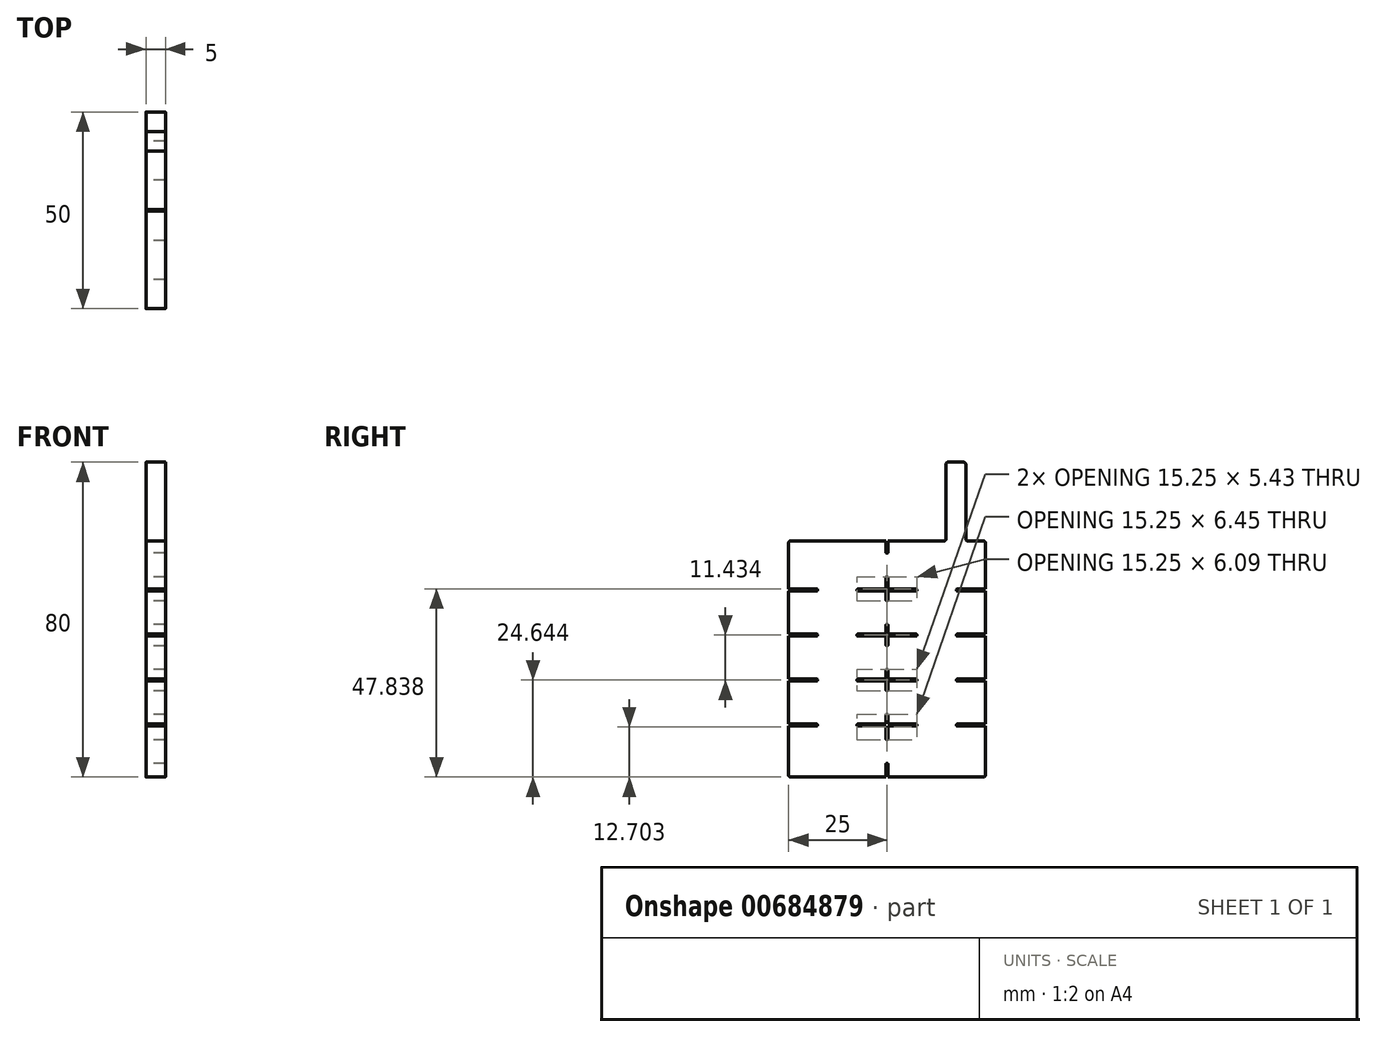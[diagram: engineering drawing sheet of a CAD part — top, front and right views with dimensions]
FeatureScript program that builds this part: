
annotation { "Feature Type Name" : "Feature", "Feature Type Description" : "" }
export const myFeature = defineFeature(function(context is Context, id is Id, definition is map)
    precondition{}
    {
        {
            var Q0;
            Q0=qCreatedBy(makeId("Right.planeOp"),FACE);
            var sketch = newSketch(context, id + "F0", { "sketchPlane" : qUnion([Q0])});
            skPoint(sketch, "E0.0", {"position": v(0, 0) * mm});
            skLineSegment(sketch, "E1.bottom", {"start": v(0, 0) * mm, "end": v(12.38, 0) * mm});
            skLineSegment(sketch, "E1.top", {"start": v(0, -60) * mm, "end": v(24.75, -60) * mm});
            skLineSegment(sketch, "E1.left", {"start": v(0, 0) * mm, "end": v(0, -12.24) * mm});
            skLineSegment(sketch, "E1.right", {"start": v(50, 0) * mm, "end": v(50, -12.24) * mm});
            skPoint(sketch, "E2.MirrorP", {"position": v(11.5, 0) * mm});
            skPoint(sketch, "E3.MirrorP", {"position": v(11.5, -2) * mm});
            skPoint(sketch, "E4.MirrorP", {"position": v(18.5, 0) * mm});
            skPoint(sketch, "E5.MirrorP", {"position": v(30, 0) * mm});
            skLineSegment(sketch, "E6.0", {"start": v(25.25, -60) * mm, "end": v(25.25, -56.52) * mm});
            skLineSegment(sketch, "E7.0", {"start": v(0, -12.24) * mm, "end": v(7.38, -12.24) * mm});
            skLineSegment(sketch, "E8.0", {"start": v(0, -12.74) * mm, "end": v(7.38, -12.74) * mm});
            skLineSegment(sketch, "E9.trimOffspring", {"start": v(25.25, -3.12) * mm, "end": v(25.25, -1.3) * mm});
            skLineSegment(sketch, "E10.trimOffspring", {"start": v(25.25, -12.24) * mm, "end": v(32.63, -12.24) * mm});
            skLineSegment(sketch, "E11.trimOffspring", {"start": v(25.25, -12.24) * mm, "end": v(25.25, -9.12) * mm});
            skLineSegment(sketch, "E12.trimOffspring", {"start": v(25.25, -12.74) * mm, "end": v(32.63, -12.74) * mm});
            skLineSegment(sketch, "E13.trimOffspring", {"start": v(25.25, -15.2) * mm, "end": v(25.25, -12.74) * mm});
            skLineSegment(sketch, "E14.0", {"start": v(0, -23.67) * mm, "end": v(7.38, -23.67) * mm});
            skLineSegment(sketch, "E15.0", {"start": v(0, -24.17) * mm, "end": v(7.38, -24.17) * mm});
            skLineSegment(sketch, "E16.trimOffspring", {"start": v(25.25, -23.67) * mm, "end": v(32.63, -23.67) * mm});
            skLineSegment(sketch, "E17.trimOffspring", {"start": v(25.25, -23.67) * mm, "end": v(25.25, -21.2) * mm});
            skLineSegment(sketch, "E18.trimOffspring", {"start": v(25.25, -24.17) * mm, "end": v(32.63, -24.17) * mm});
            skLineSegment(sketch, "E19.trimOffspring", {"start": v(25.25, -26.64) * mm, "end": v(25.25, -24.17) * mm});
            skLineSegment(sketch, "E20.trimOffspring", {"start": v(24.75, -26.64) * mm, "end": v(24.75, -24.17) * mm});
            skLineSegment(sketch, "E21.0", {"start": v(0, -35.1) * mm, "end": v(7.38, -35.1) * mm});
            skLineSegment(sketch, "E22.0", {"start": v(0, -35.6) * mm, "end": v(7.38, -35.6) * mm});
            skLineSegment(sketch, "E23.trimOffspring", {"start": v(25.25, -35.1) * mm, "end": v(32.63, -35.1) * mm});
            skLineSegment(sketch, "E24.trimOffspring", {"start": v(25.25, -35.1) * mm, "end": v(25.25, -32.64) * mm});
            skLineSegment(sketch, "E25.trimOffspring", {"start": v(24.75, -35.1) * mm, "end": v(24.75, -32.64) * mm});
            skLineSegment(sketch, "E26.trimOffspring", {"start": v(25.25, -35.6) * mm, "end": v(32.63, -35.6) * mm});
            skLineSegment(sketch, "E27.trimOffspring", {"start": v(25.25, -38.07) * mm, "end": v(25.25, -35.6) * mm});
            skLineSegment(sketch, "E28.trimOffspring", {"start": v(24.75, -38.07) * mm, "end": v(24.75, -35.6) * mm});
            skLineSegment(sketch, "E29.0", {"start": v(0, -46.54) * mm, "end": v(7.38, -46.54) * mm});
            skLineSegment(sketch, "E30.0", {"start": v(0, -47.04) * mm, "end": v(7.38, -47.04) * mm});
            skLineSegment(sketch, "E31.trimOffspring", {"start": v(25.25, -46.54) * mm, "end": v(32.63, -46.54) * mm});
            skLineSegment(sketch, "E32.trimOffspring", {"start": v(25.25, -46.54) * mm, "end": v(25.25, -44.07) * mm});
            skLineSegment(sketch, "E33.trimOffspring", {"start": v(24.75, -46.54) * mm, "end": v(24.75, -44.07) * mm});
            skLineSegment(sketch, "E34.trimOffspring", {"start": v(25.25, -47.04) * mm, "end": v(32.63, -47.04) * mm});
            skLineSegment(sketch, "E35.trimOffspring", {"start": v(25.25, -50.52) * mm, "end": v(25.25, -47.04) * mm});
            skLineSegment(sketch, "E36.trimOffspring", {"start": v(0, -12.74) * mm, "end": v(0, -23.67) * mm});
            skLineSegment(sketch, "E37.trimOffspring", {"start": v(0, -24.17) * mm, "end": v(0, -35.1) * mm});
            skLineSegment(sketch, "E38.trimOffspring", {"start": v(0, -35.6) * mm, "end": v(0, -46.54) * mm});
            skLineSegment(sketch, "E39.trimOffspring", {"start": v(0, -47.04) * mm, "end": v(0, -60) * mm});
            skLineSegment(sketch, "E40.trimOffspring", {"start": v(50, -47.04) * mm, "end": v(50, -60) * mm});
            skLineSegment(sketch, "E41.trimOffspring", {"start": v(50, -35.6) * mm, "end": v(50, -46.54) * mm});
            skLineSegment(sketch, "E42.trimOffspring", {"start": v(50, -12.74) * mm, "end": v(50, -23.67) * mm});
            skLineSegment(sketch, "E43.trimOffspring", {"start": v(50, -24.17) * mm, "end": v(50, -35.1) * mm});
            skLineSegment(sketch, "E44.0", {"start": v(17.38, -12.74) * mm, "end": v(17.38, -12.24) * mm});
            skLineSegment(sketch, "E45.0", {"start": v(7.38, -12.74) * mm, "end": v(7.38, -12.24) * mm});
            skLineSegment(sketch, "E46", {"start": v(24.75, -12.24) * mm, "end": v(24.75, -9.12) * mm});
            skLineSegment(sketch, "E47.0", {"start": v(24.75, -9.12) * mm, "end": v(25.25, -9.12) * mm});
            skLineSegment(sketch, "E48.0", {"start": v(24.75, -3.12) * mm, "end": v(25.25, -3.12) * mm});
            skLineSegment(sketch, "E49", {"start": v(24.75, -12.74) * mm, "end": v(24.75, -15.2) * mm});
            skLineSegment(sketch, "E50.0", {"start": v(24.75, -21.2) * mm, "end": v(25.25, -21.2) * mm});
            skLineSegment(sketch, "E51.0", {"start": v(24.75, -15.2) * mm, "end": v(25.25, -15.2) * mm});
            skLineSegment(sketch, "E52", {"start": v(25.25, -1.3) * mm, "end": v(25.25, 0) * mm});
            skLineSegment(sketch, "E53.trimOffspring", {"start": v(25.25, 0) * mm, "end": v(35.12, 0) * mm});
            skPoint(sketch, "E54.start.orphan", {"position": v(24.75, -6.12) * mm});
            skLineSegment(sketch, "E55", {"start": v(7.38, -12.24) * mm, "end": v(7.38, -12.74) * mm});
            skLineSegment(sketch, "E56", {"start": v(17.38, -12.24) * mm, "end": v(17.38, -12.74) * mm});
            skLineSegment(sketch, "E57.trimOffspring", {"start": v(7.38, -23.67) * mm, "end": v(7.38, -24.17) * mm});
            skLineSegment(sketch, "E58.trimOffspring", {"start": v(17.38, -23.67) * mm, "end": v(17.38, -24.17) * mm});
            skLineSegment(sketch, "E59.trimOffspring", {"start": v(7.38, -35.1) * mm, "end": v(7.38, -35.6) * mm});
            skLineSegment(sketch, "E60.trimOffspring", {"start": v(17.38, -35.1) * mm, "end": v(17.38, -35.6) * mm});
            skLineSegment(sketch, "E61.trimOffspring", {"start": v(7.38, -46.54) * mm, "end": v(7.38, -47.04) * mm});
            skLineSegment(sketch, "E62.trimOffspring", {"start": v(17.38, -46.54) * mm, "end": v(17.38, -47.04) * mm});
            skLineSegment(sketch, "E63.trimOffspring", {"start": v(17.38, -46.54) * mm, "end": v(24.75, -46.54) * mm});
            skLineSegment(sketch, "E64.trimOffspring", {"start": v(17.38, -47.04) * mm, "end": v(24.75, -47.04) * mm});
            skLineSegment(sketch, "E65.trimOffspring", {"start": v(17.38, -35.1) * mm, "end": v(24.75, -35.1) * mm});
            skLineSegment(sketch, "E66.trimOffspring", {"start": v(17.38, -35.6) * mm, "end": v(24.75, -35.6) * mm});
            skLineSegment(sketch, "E67.trimOffspring", {"start": v(17.37, -23.67) * mm, "end": v(24.75, -23.67) * mm});
            skLineSegment(sketch, "E68.trimOffspring", {"start": v(17.37, -24.17) * mm, "end": v(24.75, -24.17) * mm});
            skLineSegment(sketch, "E69.trimOffspring", {"start": v(17.38, -12.24) * mm, "end": v(24.75, -12.24) * mm});
            skPoint(sketch, "E70.start.orphan", {"position": v(12.38, -12.74) * mm});
            skPoint(sketch, "E71.orphan", {"position": v(12.38, -12.24) * mm});
            skLineSegment(sketch, "E72.trimOffspring", {"start": v(17.38, -12.74) * mm, "end": v(24.75, -12.74) * mm});
            skLineSegment(sketch, "E73.0", {"start": v(32.63, -12.24) * mm, "end": v(32.63, -12.74) * mm});
            skLineSegment(sketch, "E74.0", {"start": v(42.62, -12.24) * mm, "end": v(42.62, -12.74) * mm});
            skLineSegment(sketch, "E75.trimOffspring", {"start": v(32.63, -23.67) * mm, "end": v(32.63, -24.17) * mm});
            skLineSegment(sketch, "E76.trimOffspring", {"start": v(42.62, -23.67) * mm, "end": v(42.62, -24.17) * mm});
            skLineSegment(sketch, "E77.trimOffspring", {"start": v(32.63, -35.1) * mm, "end": v(32.63, -35.6) * mm});
            skLineSegment(sketch, "E78.trimOffspring", {"start": v(42.62, -35.1) * mm, "end": v(42.62, -35.6) * mm});
            skLineSegment(sketch, "E79.trimOffspring", {"start": v(32.63, -46.54) * mm, "end": v(32.63, -47.04) * mm});
            skLineSegment(sketch, "E80.trimOffspring", {"start": v(42.62, -46.54) * mm, "end": v(42.62, -47.04) * mm});
            skLineSegment(sketch, "E81.0", {"start": v(24.75, -26.64) * mm, "end": v(25.25, -26.64) * mm});
            skLineSegment(sketch, "E82.0", {"start": v(24.75, -32.64) * mm, "end": v(25.25, -32.64) * mm});
            skLineSegment(sketch, "E83.0", {"start": v(24.75, -38.07) * mm, "end": v(25.25, -38.07) * mm});
            skLineSegment(sketch, "E84.0", {"start": v(24.75, -44.07) * mm, "end": v(25.25, -44.07) * mm});
            skLineSegment(sketch, "E85", {"start": v(24.75, -47.04) * mm, "end": v(24.75, -50.52) * mm});
            skLineSegment(sketch, "E86.0", {"start": v(24.75, -56.52) * mm, "end": v(25.25, -56.52) * mm});
            skLineSegment(sketch, "E87.0", {"start": v(24.75, -50.52) * mm, "end": v(25.25, -50.52) * mm});
            skLineSegment(sketch, "E88.trimOffspring", {"start": v(24.75, -56.52) * mm, "end": v(24.75, -60) * mm});
            skLineSegment(sketch, "E89.trimOffspring", {"start": v(25.25, -60) * mm, "end": v(50, -60) * mm});
            skLineSegment(sketch, "E90.trimOffspring", {"start": v(42.62, -46.54) * mm, "end": v(50, -46.54) * mm});
            skLineSegment(sketch, "E91.trimOffspring", {"start": v(42.62, -47.04) * mm, "end": v(50, -47.04) * mm});
            skLineSegment(sketch, "E92.trimOffspring", {"start": v(42.62, -35.1) * mm, "end": v(50, -35.1) * mm});
            skLineSegment(sketch, "E93.trimOffspring", {"start": v(42.62, -35.6) * mm, "end": v(50, -35.6) * mm});
            skLineSegment(sketch, "E94.trimOffspring", {"start": v(42.62, -23.67) * mm, "end": v(50, -23.67) * mm});
            skLineSegment(sketch, "E95.trimOffspring", {"start": v(42.62, -24.17) * mm, "end": v(50, -24.17) * mm});
            skLineSegment(sketch, "E96.trimOffspring", {"start": v(42.62, -12.24) * mm, "end": v(50, -12.24) * mm});
            skLineSegment(sketch, "E97.trimOffspring", {"start": v(42.62, -12.74) * mm, "end": v(50, -12.74) * mm});
            skLineSegment(sketch, "E98.trimOffspring", {"start": v(24.75, -21.2) * mm, "end": v(24.75, -23.67) * mm});
            skPoint(sketch, "E99.end.orphan", {"position": v(25.25, -18.2) * mm});
            skPoint(sketch, "E99.start.orphan", {"position": v(24.75, -18.2) * mm});
            skPoint(sketch, "E100.orphan", {"position": v(25.25, -17.95) * mm});
            skPoint(sketch, "E101.end.orphan", {"position": v(25.25, -18.45) * mm});
            skLineSegment(sketch, "E102.trimOffspring", {"start": v(24.75, -3.12) * mm, "end": v(24.75, 0) * mm});
            skPoint(sketch, "E103.orphan", {"position": v(14.88, 25) * mm});
            skPoint(sketch, "E104.orphan", {"position": v(37.63, 25) * mm});
            skLineSegment(sketch, "E105.trimOffspring", {"start": v(14.88, 0) * mm, "end": v(24.75, 0) * mm});
            skLineSegment(sketch, "E106.trimOffspring", {"start": v(37.63, 0) * mm, "end": v(40, 0) * mm});
            skLineSegment(sketch, "E107", {"start": v(35.12, 0) * mm, "end": v(40, 0) * mm});
            skLineSegment(sketch, "E108.0", {"start": v(45, 0) * mm, "end": v(45, 15) * mm});
            skLineSegment(sketch, "E109.0", {"start": v(40, 0) * mm, "end": v(40, 15) * mm});
            skLineSegment(sketch, "E110", {"start": v(14.88, 0) * mm, "end": v(11.5, 0) * mm});
            skLineSegment(sketch, "E111.trimOffspring", {"start": v(45, 0) * mm, "end": v(50, 0) * mm});
            skLineSegment(sketch, "E112.0", {"start": v(40, 20) * mm, "end": v(45, 20) * mm});
            skLineSegment(sketch, "E113", {"start": v(40, 20) * mm, "end": v(40, 15) * mm});
            skLineSegment(sketch, "E114", {"start": v(45, 20) * mm, "end": v(45, 15) * mm});
            skSolve(sketch);
        }
        {
            var Q0;
            {var subQ1=sQuery(id+"F0.wireOp",EDGE,"6f222dcf-cafe-427f-96f1-de862232ba62.0");Q0=makeQuery(id+"F0.imprint","IMPRINT",FACE,{"disambiguationData":[TD([[makeQuery(id+"F0.imprint","IMPRINT",EDGE,{"derivedFrom":subQ1}),-1.0]])]});}
            var Q1;
            {var subQ1=sQuery(id+"F0.wireOp",EDGE,"9ddca581-0f96-48d2-9b8e-d0e5be099db1.trimOffspring");Q1=makeQuery(id+"F0.imprint","IMPRINT",FACE,{"disambiguationData":[TD([[makeQuery(id+"F0.imprint","IMPRINT",EDGE,{"derivedFrom":subQ1}),-1.0]])]});}
            var Q2;
            Q2=makeQuery(id+"F0.imprint","IMPRINT",FACE,{"disambiguationData":[TD([[makeQuery(id+"F0.imprint","IMPRINT",EDGE,{"derivedFrom":sQuery(id+"F0.wireOp",EDGE,"E8.0")}),-1.0]])]});
            var Q3;
            Q3=makeQuery(id+"F0.imprint","IMPRINT",FACE,{"disambiguationData":[TD([[makeQuery(id+"F0.imprint","IMPRINT",EDGE,{"derivedFrom":sQuery(id+"F0.wireOp",EDGE,"E12.trimOffspring")}),-1.0]])]});
            var Q4;
            Q4=makeQuery(id+"F0.imprint","IMPRINT",FACE,{"disambiguationData":[TD([[makeQuery(id+"F0.imprint","IMPRINT",EDGE,{"derivedFrom":sQuery(id+"F0.wireOp",EDGE,"E18.trimOffspring")}),-1.0]])]});
            var Q5;
            Q5=makeQuery(id+"F0.imprint","IMPRINT",FACE,{"disambiguationData":[TD([[makeQuery(id+"F0.imprint","IMPRINT",EDGE,{"derivedFrom":sQuery(id+"F0.wireOp",EDGE,"E15.0")}),-1.0]])]});
            var Q6;
            Q6=makeQuery(id+"F0.imprint","IMPRINT",FACE,{"disambiguationData":[TD([[makeQuery(id+"F0.imprint","IMPRINT",EDGE,{"derivedFrom":sQuery(id+"F0.wireOp",EDGE,"E22.0")}),-1.0]])]});
            var Q7;
            Q7=makeQuery(id+"F0.imprint","IMPRINT",FACE,{"disambiguationData":[TD([[makeQuery(id+"F0.imprint","IMPRINT",EDGE,{"derivedFrom":sQuery(id+"F0.wireOp",EDGE,"E26.trimOffspring")}),-1.0]])]});
            var Q8;
            {var subQ0=sQuery(id+"F0.wireOp",EDGE,"E6.0");Q8=makeQuery(id+"F0.imprint","IMPRINT",FACE,{"disambiguationData":[TD([[makeQuery(id+"F0.imprint","IMPRINT",EDGE,{"derivedFrom":subQ0}),-1.0]])]});}
            var Q9;
            {var subQ0=sQuery(id+"F0.wireOp",EDGE,"52d86100-12cc-4532-affd-39e9c9b04a49.0");Q9=makeQuery(id+"F0.imprint","IMPRINT",FACE,{"disambiguationData":[TD([[makeQuery(id+"F0.imprint","IMPRINT",EDGE,{"derivedFrom":subQ0}),1.0]])]});}
            extrude(context, id + "F1", {"entities" : qUnion([Q0, Q1, Q2, Q3, Q4, Q5, Q6, Q7, Q8, Q9]), "depth" : 5 * mm, "offsetDistance" : 25 * mm});
        }
        {
            var Q0;
            Q0=makeQuery(id+"F1.opExtrude","SWEPT_EDGE",EDGE,{"disambiguationData":[OSD([sQuery(id+"F0.wireOp",EDGE,"E1.bottom"),sQuery(id+"F0.wireOp",EDGE,"E1.left")])]});
            var Q1;
            Q1=makeQuery(id+"F1.opExtrude","SWEPT_EDGE",EDGE,{"disambiguationData":[OSD([sQuery(id+"F0.wireOp",EDGE,"E1.right"),sQuery(id+"F0.wireOp",EDGE,"E111.trimOffspring")])]});
            var Q2;
            Q2=makeQuery(id+"F1.opExtrude","SWEPT_EDGE",EDGE,{"disambiguationData":[OSD([sQuery(id+"F0.wireOp",EDGE,"E40.trimOffspring"),sQuery(id+"F0.wireOp",EDGE,"E89.trimOffspring")])]});
            var Q3;
            Q3=makeQuery(id+"F1.opExtrude","SWEPT_EDGE",EDGE,{"disambiguationData":[OSD([sQuery(id+"F0.wireOp",EDGE,"E1.top"),sQuery(id+"F0.wireOp",EDGE,"E39.trimOffspring")])]});
            fillet(context, id + "F2", {"entities" : qUnion([Q0, Q1, Q2, Q3]), "radius" : 0.5 * mm, "tangentPropagation" : true, "allowEdgeOverflow" : false});
        }
        {
            var Q0;
            Q0=makeQuery(id+"F1.opExtrude","SWEPT_EDGE",EDGE,{"disambiguationData":[OSD([sQuery(id+"F0.wireOp",EDGE,"E112.0"),sQuery(id+"F0.wireOp",EDGE,"E114")])]});
            var Q1;
            Q1=makeQuery(id+"F1.opExtrude","SWEPT_EDGE",EDGE,{"disambiguationData":[OSD([sQuery(id+"F0.wireOp",EDGE,"E112.0"),sQuery(id+"F0.wireOp",EDGE,"E113")])]});
            fillet(context, id + "F3", {"entities" : qUnion([Q0, Q1]), "radius" : 0.5 * mm, "tangentPropagation" : true, "allowEdgeOverflow" : false});
        }
        {
            var Q0;
            Q0=makeQuery(id+"F1.opExtrude","SWEPT_EDGE",EDGE,{"disambiguationData":[OSD([sQuery(id+"F0.wireOp",EDGE,"E107"),sQuery(id+"F0.wireOp",EDGE,"E109.0")])]});
            var Q1;
            Q1=makeQuery(id+"F1.opExtrude","SWEPT_EDGE",EDGE,{"disambiguationData":[OSD([sQuery(id+"F0.wireOp",EDGE,"E108.0"),sQuery(id+"F0.wireOp",EDGE,"E111.trimOffspring")])]});
            fillet(context, id + "F4", {"entities" : qUnion([Q0, Q1]), "radius" : 0.5 * mm, "tangentPropagation" : true, "allowEdgeOverflow" : false});
        }
        {
            var Q0;
            Q0=makeQuery(id+"F1.opExtrude","SWEPT_EDGE",EDGE,{"disambiguationData":[OSD([sQuery(id+"F0.wireOp",EDGE,"E9.trimOffspring"),sQuery(id+"F0.wireOp",EDGE,"E48.0")])]});
            var Q1;
            Q1=makeQuery(id+"F1.opExtrude","SWEPT_EDGE",EDGE,{"disambiguationData":[OSD([sQuery(id+"F0.wireOp",EDGE,"E48.0"),sQuery(id+"F0.wireOp",EDGE,"E102.trimOffspring")])]});
            var Q2;
            Q2=makeQuery(id+"F1.opExtrude","SWEPT_EDGE",EDGE,{"disambiguationData":[OSD([sQuery(id+"F0.wireOp",EDGE,"E74.0"),sQuery(id+"F0.wireOp",EDGE,"E96.trimOffspring")])]});
            var Q3;
            Q3=makeQuery(id+"F1.opExtrude","SWEPT_EDGE",EDGE,{"disambiguationData":[OSD([sQuery(id+"F0.wireOp",EDGE,"E74.0"),sQuery(id+"F0.wireOp",EDGE,"E97.trimOffspring")])]});
            var Q4;
            Q4=makeQuery(id+"F1.opExtrude","SWEPT_EDGE",EDGE,{"disambiguationData":[OSD([sQuery(id+"F0.wireOp",EDGE,"E76.trimOffspring"),sQuery(id+"F0.wireOp",EDGE,"E94.trimOffspring")])]});
            var Q5;
            Q5=makeQuery(id+"F1.opExtrude","SWEPT_EDGE",EDGE,{"disambiguationData":[OSD([sQuery(id+"F0.wireOp",EDGE,"E76.trimOffspring"),sQuery(id+"F0.wireOp",EDGE,"E95.trimOffspring")])]});
            var Q6;
            Q6=makeQuery(id+"F1.opExtrude","SWEPT_EDGE",EDGE,{"disambiguationData":[OSD([sQuery(id+"F0.wireOp",EDGE,"E78.trimOffspring"),sQuery(id+"F0.wireOp",EDGE,"E92.trimOffspring")])]});
            var Q7;
            Q7=makeQuery(id+"F1.opExtrude","SWEPT_EDGE",EDGE,{"disambiguationData":[OSD([sQuery(id+"F0.wireOp",EDGE,"E78.trimOffspring"),sQuery(id+"F0.wireOp",EDGE,"E93.trimOffspring")])]});
            var Q8;
            Q8=makeQuery(id+"F1.opExtrude","SWEPT_EDGE",EDGE,{"disambiguationData":[OSD([sQuery(id+"F0.wireOp",EDGE,"E80.trimOffspring"),sQuery(id+"F0.wireOp",EDGE,"E90.trimOffspring")])]});
            var Q9;
            Q9=makeQuery(id+"F1.opExtrude","SWEPT_EDGE",EDGE,{"disambiguationData":[OSD([sQuery(id+"F0.wireOp",EDGE,"E80.trimOffspring"),sQuery(id+"F0.wireOp",EDGE,"E91.trimOffspring")])]});
            var Q10;
            Q10=makeQuery(id+"F1.opExtrude","SWEPT_EDGE",EDGE,{"disambiguationData":[OSD([sQuery(id+"F0.wireOp",EDGE,"E86.0"),sQuery(id+"F0.wireOp",EDGE,"E88.trimOffspring")])]});
            var Q11;
            Q11=makeQuery(id+"F1.opExtrude","SWEPT_EDGE",EDGE,{"disambiguationData":[OSD([sQuery(id+"F0.wireOp",EDGE,"E6.0"),sQuery(id+"F0.wireOp",EDGE,"E86.0")])]});
            var Q12;
            Q12=makeQuery(id+"F1.opExtrude","SWEPT_EDGE",EDGE,{"disambiguationData":[OSD([sQuery(id+"F0.wireOp",EDGE,"E85"),sQuery(id+"F0.wireOp",EDGE,"E87.0")])]});
            var Q13;
            Q13=makeQuery(id+"F1.opExtrude","SWEPT_EDGE",EDGE,{"disambiguationData":[OSD([sQuery(id+"F0.wireOp",EDGE,"E35.trimOffspring"),sQuery(id+"F0.wireOp",EDGE,"E87.0")])]});
            var Q14;
            Q14=makeQuery(id+"F1.opExtrude","SWEPT_EDGE",EDGE,{"disambiguationData":[OSD([sQuery(id+"F0.wireOp",EDGE,"E34.trimOffspring"),sQuery(id+"F0.wireOp",EDGE,"E79.trimOffspring")])]});
            var Q15;
            Q15=makeQuery(id+"F1.opExtrude","SWEPT_EDGE",EDGE,{"disambiguationData":[OSD([sQuery(id+"F0.wireOp",EDGE,"E31.trimOffspring"),sQuery(id+"F0.wireOp",EDGE,"E79.trimOffspring")])]});
            var Q16;
            Q16=makeQuery(id+"F1.opExtrude","SWEPT_EDGE",EDGE,{"disambiguationData":[OSD([sQuery(id+"F0.wireOp",EDGE,"E32.trimOffspring"),sQuery(id+"F0.wireOp",EDGE,"E84.0")])]});
            var Q17;
            Q17=makeQuery(id+"F1.opExtrude","SWEPT_EDGE",EDGE,{"disambiguationData":[OSD([sQuery(id+"F0.wireOp",EDGE,"E33.trimOffspring"),sQuery(id+"F0.wireOp",EDGE,"E84.0")])]});
            var Q18;
            Q18=makeQuery(id+"F1.opExtrude","SWEPT_EDGE",EDGE,{"disambiguationData":[OSD([sQuery(id+"F0.wireOp",EDGE,"E62.trimOffspring"),sQuery(id+"F0.wireOp",EDGE,"E63.trimOffspring")])]});
            var Q19;
            Q19=makeQuery(id+"F1.opExtrude","SWEPT_EDGE",EDGE,{"disambiguationData":[OSD([sQuery(id+"F0.wireOp",EDGE,"E62.trimOffspring"),sQuery(id+"F0.wireOp",EDGE,"E64.trimOffspring")])]});
            var Q20;
            Q20=makeQuery(id+"F1.opExtrude","SWEPT_EDGE",EDGE,{"disambiguationData":[OSD([sQuery(id+"F0.wireOp",EDGE,"E28.trimOffspring"),sQuery(id+"F0.wireOp",EDGE,"E83.0")])]});
            var Q21;
            Q21=makeQuery(id+"F1.opExtrude","SWEPT_EDGE",EDGE,{"disambiguationData":[OSD([sQuery(id+"F0.wireOp",EDGE,"E27.trimOffspring"),sQuery(id+"F0.wireOp",EDGE,"E83.0")])]});
            var Q22;
            Q22=makeQuery(id+"F1.opExtrude","SWEPT_EDGE",EDGE,{"disambiguationData":[OSD([sQuery(id+"F0.wireOp",EDGE,"E26.trimOffspring"),sQuery(id+"F0.wireOp",EDGE,"E77.trimOffspring")])]});
            var Q23;
            Q23=makeQuery(id+"F1.opExtrude","SWEPT_EDGE",EDGE,{"disambiguationData":[OSD([sQuery(id+"F0.wireOp",EDGE,"E23.trimOffspring"),sQuery(id+"F0.wireOp",EDGE,"E77.trimOffspring")])]});
            var Q24;
            Q24=makeQuery(id+"F1.opExtrude","SWEPT_EDGE",EDGE,{"disambiguationData":[OSD([sQuery(id+"F0.wireOp",EDGE,"E24.trimOffspring"),sQuery(id+"F0.wireOp",EDGE,"E82.0")])]});
            var Q25;
            Q25=makeQuery(id+"F1.opExtrude","SWEPT_EDGE",EDGE,{"disambiguationData":[OSD([sQuery(id+"F0.wireOp",EDGE,"E25.trimOffspring"),sQuery(id+"F0.wireOp",EDGE,"E82.0")])]});
            var Q26;
            Q26=makeQuery(id+"F1.opExtrude","SWEPT_EDGE",EDGE,{"disambiguationData":[OSD([sQuery(id+"F0.wireOp",EDGE,"E60.trimOffspring"),sQuery(id+"F0.wireOp",EDGE,"E66.trimOffspring")])]});
            var Q27;
            Q27=makeQuery(id+"F1.opExtrude","SWEPT_EDGE",EDGE,{"disambiguationData":[OSD([sQuery(id+"F0.wireOp",EDGE,"E60.trimOffspring"),sQuery(id+"F0.wireOp",EDGE,"E65.trimOffspring")])]});
            var Q28;
            Q28=makeQuery(id+"F1.opExtrude","SWEPT_EDGE",EDGE,{"disambiguationData":[OSD([sQuery(id+"F0.wireOp",EDGE,"E58.trimOffspring"),sQuery(id+"F0.wireOp",EDGE,"E67.trimOffspring")])]});
            var Q29;
            Q29=makeQuery(id+"F1.opExtrude","SWEPT_EDGE",EDGE,{"disambiguationData":[OSD([sQuery(id+"F0.wireOp",EDGE,"E58.trimOffspring"),sQuery(id+"F0.wireOp",EDGE,"E68.trimOffspring")])]});
            var Q30;
            Q30=makeQuery(id+"F1.opExtrude","SWEPT_EDGE",EDGE,{"disambiguationData":[OSD([sQuery(id+"F0.wireOp",EDGE,"E20.trimOffspring"),sQuery(id+"F0.wireOp",EDGE,"E81.0")])]});
            var Q31;
            Q31=makeQuery(id+"F1.opExtrude","SWEPT_EDGE",EDGE,{"disambiguationData":[OSD([sQuery(id+"F0.wireOp",EDGE,"E19.trimOffspring"),sQuery(id+"F0.wireOp",EDGE,"E81.0")])]});
            var Q32;
            Q32=makeQuery(id+"F1.opExtrude","SWEPT_EDGE",EDGE,{"disambiguationData":[OSD([sQuery(id+"F0.wireOp",EDGE,"E18.trimOffspring"),sQuery(id+"F0.wireOp",EDGE,"E75.trimOffspring")])]});
            var Q33;
            Q33=makeQuery(id+"F1.opExtrude","SWEPT_EDGE",EDGE,{"disambiguationData":[OSD([sQuery(id+"F0.wireOp",EDGE,"E16.trimOffspring"),sQuery(id+"F0.wireOp",EDGE,"E75.trimOffspring")])]});
            var Q34;
            Q34=makeQuery(id+"F1.opExtrude","SWEPT_EDGE",EDGE,{"disambiguationData":[OSD([sQuery(id+"F0.wireOp",EDGE,"E17.trimOffspring"),sQuery(id+"F0.wireOp",EDGE,"E50.0")])]});
            var Q35;
            Q35=makeQuery(id+"F1.opExtrude","SWEPT_EDGE",EDGE,{"disambiguationData":[OSD([sQuery(id+"F0.wireOp",EDGE,"E50.0"),sQuery(id+"F0.wireOp",EDGE,"E98.trimOffspring")])]});
            var Q36;
            Q36=makeQuery(id+"F1.opExtrude","SWEPT_EDGE",EDGE,{"disambiguationData":[OSD([sQuery(id+"F0.wireOp",EDGE,"E56"),sQuery(id+"F0.wireOp",EDGE,"E69.trimOffspring")])]});
            var Q37;
            Q37=makeQuery(id+"F1.opExtrude","SWEPT_EDGE",EDGE,{"disambiguationData":[OSD([sQuery(id+"F0.wireOp",EDGE,"E56"),sQuery(id+"F0.wireOp",EDGE,"E72.trimOffspring")])]});
            var Q38;
            Q38=makeQuery(id+"F1.opExtrude","SWEPT_EDGE",EDGE,{"disambiguationData":[OSD([sQuery(id+"F0.wireOp",EDGE,"E49"),sQuery(id+"F0.wireOp",EDGE,"E51.0")])]});
            var Q39;
            Q39=makeQuery(id+"F1.opExtrude","SWEPT_EDGE",EDGE,{"disambiguationData":[OSD([sQuery(id+"F0.wireOp",EDGE,"E13.trimOffspring"),sQuery(id+"F0.wireOp",EDGE,"E51.0")])]});
            var Q40;
            Q40=makeQuery(id+"F1.opExtrude","SWEPT_EDGE",EDGE,{"disambiguationData":[OSD([sQuery(id+"F0.wireOp",EDGE,"E12.trimOffspring"),sQuery(id+"F0.wireOp",EDGE,"E73.0")])]});
            var Q41;
            Q41=makeQuery(id+"F1.opExtrude","SWEPT_EDGE",EDGE,{"disambiguationData":[OSD([sQuery(id+"F0.wireOp",EDGE,"E10.trimOffspring"),sQuery(id+"F0.wireOp",EDGE,"E73.0")])]});
            var Q42;
            Q42=makeQuery(id+"F1.opExtrude","SWEPT_EDGE",EDGE,{"disambiguationData":[OSD([sQuery(id+"F0.wireOp",EDGE,"E11.trimOffspring"),sQuery(id+"F0.wireOp",EDGE,"E47.0")])]});
            var Q43;
            Q43=makeQuery(id+"F1.opExtrude","SWEPT_EDGE",EDGE,{"disambiguationData":[OSD([sQuery(id+"F0.wireOp",EDGE,"E46"),sQuery(id+"F0.wireOp",EDGE,"E47.0")])]});
            var Q44;
            Q44=makeQuery(id+"F1.opExtrude","SWEPT_EDGE",EDGE,{"disambiguationData":[OSD([sQuery(id+"F0.wireOp",EDGE,"E8.0"),sQuery(id+"F0.wireOp",EDGE,"E55")])]});
            var Q45;
            Q45=makeQuery(id+"F1.opExtrude","SWEPT_EDGE",EDGE,{"disambiguationData":[OSD([sQuery(id+"F0.wireOp",EDGE,"E15.0"),sQuery(id+"F0.wireOp",EDGE,"E57.trimOffspring")])]});
            var Q46;
            Q46=makeQuery(id+"F1.opExtrude","SWEPT_EDGE",EDGE,{"disambiguationData":[OSD([sQuery(id+"F0.wireOp",EDGE,"E7.0"),sQuery(id+"F0.wireOp",EDGE,"E55")])]});
            var Q47;
            Q47=makeQuery(id+"F1.opExtrude","SWEPT_EDGE",EDGE,{"disambiguationData":[OSD([sQuery(id+"F0.wireOp",EDGE,"E14.0"),sQuery(id+"F0.wireOp",EDGE,"E57.trimOffspring")])]});
            var Q48;
            Q48=makeQuery(id+"F1.opExtrude","SWEPT_EDGE",EDGE,{"disambiguationData":[OSD([sQuery(id+"F0.wireOp",EDGE,"E29.0"),sQuery(id+"F0.wireOp",EDGE,"E61.trimOffspring")])]});
            var Q49;
            Q49=makeQuery(id+"F1.opExtrude","SWEPT_EDGE",EDGE,{"disambiguationData":[OSD([sQuery(id+"F0.wireOp",EDGE,"E21.0"),sQuery(id+"F0.wireOp",EDGE,"E59.trimOffspring")])]});
            var Q50;
            Q50=makeQuery(id+"F1.opExtrude","SWEPT_EDGE",EDGE,{"disambiguationData":[OSD([sQuery(id+"F0.wireOp",EDGE,"E22.0"),sQuery(id+"F0.wireOp",EDGE,"E59.trimOffspring")])]});
            var Q51;
            Q51=makeQuery(id+"F1.opExtrude","SWEPT_EDGE",EDGE,{"disambiguationData":[OSD([sQuery(id+"F0.wireOp",EDGE,"E30.0"),sQuery(id+"F0.wireOp",EDGE,"E61.trimOffspring")])]});
            fillet(context, id + "F5", {"entities" : qUnion([Q0, Q1, Q2, Q3, Q4, Q5, Q6, Q7, Q8, Q9, Q10, Q11, Q12, Q13, Q14, Q15, Q16, Q17, Q18, Q19, Q20, Q21, Q22, Q23, Q24, Q25, Q26, Q27, Q28, Q29, Q30, Q31, Q32, Q33, Q34, Q35, Q36, Q37, Q38, Q39, Q40, Q41, Q42, Q43, Q44, Q45, Q46, Q47, Q48, Q49, Q50, Q51]), "radius" : 0.2 * mm, "tangentPropagation" : true, "allowEdgeOverflow" : false});
        }
    });
